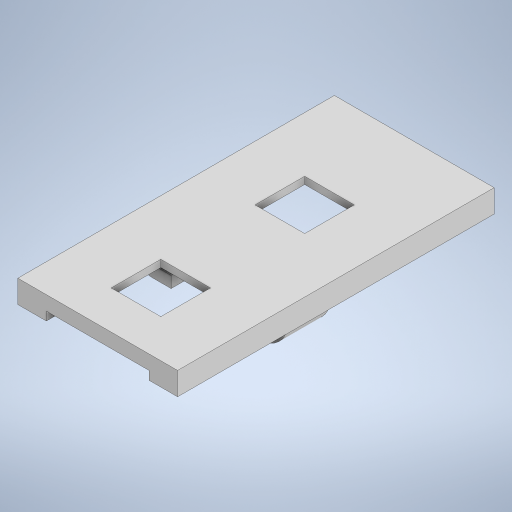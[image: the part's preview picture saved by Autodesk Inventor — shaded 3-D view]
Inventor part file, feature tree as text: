
AUTODESK INVENTOR PART (.ipt)
format: ipt  version: 2023 (Build 270158000, 158)  size: 658,944 bytes
history: native  units: in
note: dims shown in document units (in); Inventor stores cm internally (conversion verified against a paired STEP export)
features: extrude x17, sketch x15, fillet x2
ambient origin geometry x8: Origin, YZ Plane, XZ Plane, XY Plane, X Axis, Y Axis, Z Axis, Center Point
bodies: Solid1 (feature_tree)
feature tree (34):
  extrude  "Extrusion1"  Depth=4.5in
  extrude  "Extrusion2"  Depth=0.2in
  fillet  "Fillet1"  Radius=1.4in
  extrude  "Extrusion3"  Depth=0.125in
  extrude  "Extrusion4"  Depth=2.2875in
  extrude  "Extrusion5"  Depth=0.5437in
  sketch  "Sketch6"  dims[d13=0.75in d14=1.4in d15=0.0in]
  extrude  "Extrusion6"  Depth=1.4in TaperAngle=0.0deg
  extrude  "Extrusion9"  Depth=0.1in
  extrude  "Extrusion10"  Depth=0.1in
  extrude  "Extrusion11"  Depth=0.25in
  extrude  "Extrusion12"  Depth=0.15in
  extrude  "Extrusion13"  Depth=0.7in
  extrude  "Extrusion14"  Depth=0.1in
  extrude  "Extrusion15"  Depth=0.615in
  extrude  "Extrusion16"  Depth=1.1in
  fillet  "Fillet2"  Radius=0.21in
  extrude  "Extrusion18"  Depth=0.5in
  extrude  "Extrusion19"  Depth=0.5in
  extrude  "Extrusion20"  Depth=0.5in
  sketch  "Sketch1"  dims[d0=7.0in d1=4.5in]
  sketch  "Sketch2"  dims[d2=1.5in d3=0.0in d4=0.2in d5=1.4in d6=0.0in]
  sketch  "Sketch3"  dims[d7=0.125in d8=0.25in]
  sketch  "Sketch4"  dims[d9=0.25in d10=2.2875in]
  sketch  "Sketch5"  dims[d11=3.4125in d12=0.5437in]
  sketch  "Sketch8"  dims[d16=0.1in d17=0.14in]
  sketch  "Sketch9"  dims[d18=0.1in d19=0.275in]
  sketch  "Sketch10"  dims[d20=0.35in d21=0.25in]
  sketch  "Sketch11"  dims[d22=0.15in d23=0.15in]
  sketch  "Sketch12"  dims[d24=0.25in d25=0.7in]
  sketch  "Sketch13"  dims[d26=0.1in d27=0.1in]
  sketch  "Sketch15"  dims[d28=0.25in d29=0.615in]
  sketch  "Sketch16"  dims[d30=0.25in d31=1.1in d32=0.21in]
  sketch  "Sketch17"  dims[d33=0.3075in d34=0.5575in d35=1.65in d36=0.3075in d37=0.21in d38=0.5575in d39=2.1in d40=0.1in d41=0.1in d42=0.3in d43=0.1in d44=0.25in d45=0.615in d46=2.4in d47=0.11in d48=2.51in d49=0.5575in d50=0.1in d51=0.615in d52=0.175in d53=0.175in d54=0.1in d55=0.1in d56=0.25in d57=3.15in d58=0.1in d59=0.515in d60=0.05in d61=0.0in d62=0.1562in d63=0.1562in d64=0.2175in d65=0.2175in d66=0.2175in d67=0.2175in d68=0.2175in d69=0.2175in d70=0.63in d71=0.63in d72=0.63in d73=0.63in d74=0.8812in d76=2.25in d77=0.3in d78=0.3in d79=0.3in d80=0.3in d81=0.3in d82=0.625in d83=0.625in d84=0.625in d85=0.625in d86=1.0in d87=3.1in d88=3.1in d89=3.1in d90=3.1in d91=3.1in d92=1.0in d93=0.0in d97=0.4in d98=0.4in d99=0.4in d100=0.4in d101=0.4in d102=0.05in d103=0.0in d124=0.0688in d125=0.0in d126=0.25in d127=0.275in d128=0.25in d129=0.25in d130=0.25in d131=2.1in d132=0.125in d133=0.0625in d134=0.05in d135=0.0in d142=0.0375in d143=0.0in d144=2.0in d145=0.78in d146=0.0725in d147=0.3in d148=0.14in d149=0.1in d150=0.7in d151=0.2in d152=0.0in d153=0.075in d154=0.125in d155=0.0in d156=0.28in d157=2.5in d158=0.49in d159=0.25in d160=0.0in d161=0.45in d162=0.081in d163=0.0in d164=0.45in d177=0.075in d178=0.0in d179=0.125in d187=2.8in d189=0.04in d190=0.04in d191=0.04in d192=0.04in d193=0.04in d194=0.45in d195=0.0765in d196=0.076in d197=3.325in d198=0.254in d199=0.2535in d202=0.075in d203=0.125in d204=0.075in d205=0.125in d206=0.1875in d207=0.1875in d208=0.1875in d209=0.65in d210=0.65in d211=0.65in d212=0.125in d213=0.075in d214=0.025in d215=2.0in d216=0.5in d217=0.0in d218=0.0in d219=0.28in d220=0.14in d221=0.245in d222=0.28in d223=7.0in d224=0.0in d225=7.0in d226=0.0in]
